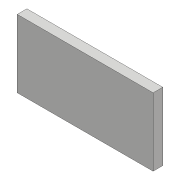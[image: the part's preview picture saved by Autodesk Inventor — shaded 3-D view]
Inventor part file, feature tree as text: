
AUTODESK INVENTOR PART (.ipt)
format: ipt  version: 2018 (Build 220112000, 112)  size: 72,704 bytes
history: native  units: mm
features: extrude x1, sketch x1
ambient origin geometry x8: Origin, YZ Plane, XZ Plane, XY Plane, X Axis, Y Axis, Z Axis, Center Point
bodies: Solid1 (feature_tree)
feature tree (2):
  extrude  "Extrusion1"  Depth=50.8mm
  sketch  "Sketch1"  dims[d0=25.4mm d1=50.8mm d2=3.6mm d3=0.0mm]
